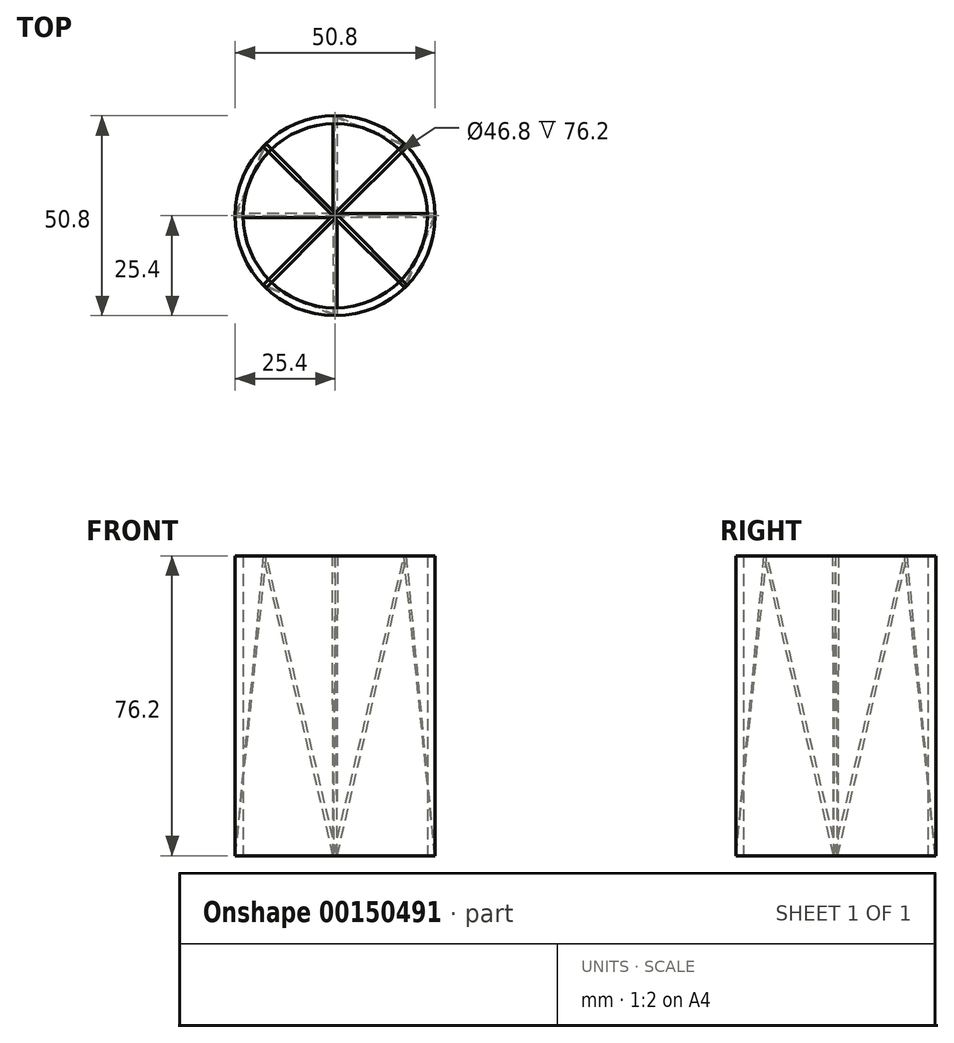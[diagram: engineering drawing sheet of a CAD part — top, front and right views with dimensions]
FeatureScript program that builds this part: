
annotation { "Feature Type Name" : "Feature", "Feature Type Description" : "" }
export const myFeature = defineFeature(function(context is Context, id is Id, definition is map)
    precondition{}
    {
        {
            var Q0;
            Q0=qCreatedBy(makeId("Top.planeOp"),FACE);
            var sketch = newSketch(context, id + "F0", { "sketchPlane" : qUnion([Q0])});
            skCircle(sketch, "E0", {"center": v(0, 0) * mm, "radius": 23.4 * mm});
            skCircle(sketch, "E1", {"center": v(0, 0) * mm, "radius": 25.4 * mm});
            skSolve(sketch);
        }
        {
            var Q0;
            Q0=makeQuery(id+"F0.imprint","IMPRINT",FACE,{"disambiguationData":[TD([[makeQuery(id+"F0.imprint","IMPRINT",EDGE,{"derivedFrom":sQuery(id+"F0.wireOp",EDGE,"E0")}),-1.0]])]});
            extrude(context, id + "F1", {"entities" : qUnion([Q0]), "depth" : 76.2 * mm});
        }
        {
            var Q0;
            Q0=qCreatedBy(makeId("Top.planeOp"),FACE);
            var sketch = newSketch(context, id + "F2", { "sketchPlane" : qUnion([Q0])});
            skLineSegment(sketch, "E2.bottom", {"start": v(-0.5, 25.31) * mm, "end": v(0.5, 25.31) * mm});
            skLineSegment(sketch, "E2.top", {"start": v(-0.5, -25.31) * mm, "end": v(0.5, -25.31) * mm});
            skLineSegment(sketch, "E2.left", {"start": v(-0.5, 25.31) * mm, "end": v(-0.5, -25.31) * mm});
            skLineSegment(sketch, "E2.right", {"start": v(0.5, 25.32) * mm, "end": v(0.5, -25.31) * mm});
            skPoint(sketch, "E2.middle", {"position": v(0, 0) * mm});
            skLineSegment(sketch, "E3.bottom", {"start": v(25.32, 0.5) * mm, "end": v(-25.32, 0.5) * mm});
            skLineSegment(sketch, "E3.top", {"start": v(25.32, -0.5) * mm, "end": v(-25.32, -0.5) * mm});
            skLineSegment(sketch, "E3.left", {"start": v(25.32, 0.5) * mm, "end": v(25.32, -0.5) * mm});
            skLineSegment(sketch, "E4", {"start": v(-25.32, 0.5) * mm, "end": v(-25.32, -0.5) * mm});
            skSolve(sketch);
        }
        {
            var Q0;
            Q0=qCreatedBy(makeId("Top.planeOp"),FACE);
            cPlane(context, id + "F3", {"entities" : qUnion([Q0]), "cplaneType" : CPlaneType.OFFSET, "offset" : 76.2 * mm, "width" : 152.4 * mm, "height" : 152.4 * mm});
        }
        {
            var Q0;
            Q0=qCreatedBy(id+"F3.planeOp",FACE);
            var sketch = newSketch(context, id + "F4", { "sketchPlane" : qUnion([Q0])});
            skLineSegment(sketch, "E5.bottom", {"start": v(-18.17, 17.46) * mm, "end": v(-17.46, 18.17) * mm});
            skLineSegment(sketch, "E5.top", {"start": v(17.46, -18.17) * mm, "end": v(18.17, -17.46) * mm});
            skLineSegment(sketch, "E5.left", {"start": v(-18.17, 17.46) * mm, "end": v(17.46, -18.17) * mm});
            skLineSegment(sketch, "E5.right", {"start": v(-17.46, 18.17) * mm, "end": v(18.17, -17.46) * mm});
            skPoint(sketch, "E5.middle", {"position": v(0, 0) * mm});
            skLineSegment(sketch, "E6.bottom", {"start": v(17.5, 18.2) * mm, "end": v(-18.2, -17.5) * mm});
            skLineSegment(sketch, "E6.top", {"start": v(18.2, 17.5) * mm, "end": v(-17.5, -18.2) * mm});
            skLineSegment(sketch, "E6.left", {"start": v(17.5, 18.2) * mm, "end": v(18.2, 17.5) * mm});
            skLineSegment(sketch, "E6.right", {"start": v(-18.2, -17.5) * mm, "end": v(-17.5, -18.2) * mm});
            skSolve(sketch);
        }
        {
            var Q0;
            {var subQ0=sQuery(id+"F2.wireOp",EDGE,"E2.top");Q0=makeQuery(id+"F2.imprint","IMPRINT",FACE,{"disambiguationData":[TD([[makeQuery(id+"F2.imprint","IMPRINT",EDGE,{"derivedFrom":subQ0}),1.0]])]});}
            var Q1;
            {var subQ5=sQuery(id+"F4.wireOp",EDGE,"E6.right");Q1=makeQuery(id+"F4.imprint","IMPRINT",FACE,{"disambiguationData":[TD([[makeQuery(id+"F4.imprint","IMPRINT",EDGE,{"derivedFrom":subQ5}),1.0]])]});}
            loft(context, id + "F5", {"sheetProfilesArray" : [{ "sheetProfileEntities" : qUnion([Q0]) }, { "sheetProfileEntities" : qUnion([Q1]) }]});
        }
        {
            var Q0;
            {var subQ5=sQuery(id+"F2.wireOp",EDGE,"E4");Q0=makeQuery(id+"F2.imprint","IMPRINT",FACE,{"disambiguationData":[TD([[makeQuery(id+"F2.imprint","IMPRINT",EDGE,{"derivedFrom":subQ5}),1.0]])]});}
            var Q1;
            {var subQ0=sQuery(id+"F4.wireOp",EDGE,"E5.bottom");Q1=makeQuery(id+"F4.imprint","IMPRINT",FACE,{"disambiguationData":[TD([[makeQuery(id+"F4.imprint","IMPRINT",EDGE,{"derivedFrom":subQ0}),-1.0]])]});}
            loft(context, id + "F6", {"sheetProfilesArray" : [{ "sheetProfileEntities" : qUnion([Q0]) }, { "sheetProfileEntities" : qUnion([Q1]) }]});
        }
        {
            var Q0;
            {var subQ0=sQuery(id+"F2.wireOp",EDGE,"E2.bottom");Q0=makeQuery(id+"F2.imprint","IMPRINT",FACE,{"disambiguationData":[TD([[makeQuery(id+"F2.imprint","IMPRINT",EDGE,{"derivedFrom":subQ0}),-1.0]])]});}
            var Q1;
            {var subQ5=sQuery(id+"F4.wireOp",EDGE,"E6.left");Q1=makeQuery(id+"F4.imprint","IMPRINT",FACE,{"disambiguationData":[TD([[makeQuery(id+"F4.imprint","IMPRINT",EDGE,{"derivedFrom":subQ5}),-1.0]])]});}
            loft(context, id + "F7", {"sheetProfilesArray" : [{ "sheetProfileEntities" : qUnion([Q0]) }, { "sheetProfileEntities" : qUnion([Q1]) }]});
        }
        {
            var Q0;
            {var subQ5=sQuery(id+"F2.wireOp",EDGE,"E3.left");Q0=makeQuery(id+"F2.imprint","IMPRINT",FACE,{"disambiguationData":[TD([[makeQuery(id+"F2.imprint","IMPRINT",EDGE,{"derivedFrom":subQ5}),-1.0]])]});}
            var Q1;
            {var subQ0=sQuery(id+"F4.wireOp",EDGE,"E5.top");Q1=makeQuery(id+"F4.imprint","IMPRINT",FACE,{"disambiguationData":[TD([[makeQuery(id+"F4.imprint","IMPRINT",EDGE,{"derivedFrom":subQ0}),1.0]])]});}
            loft(context, id + "F8", {"sheetProfilesArray" : [{ "sheetProfileEntities" : qUnion([Q0]) }, { "sheetProfileEntities" : qUnion([Q1]) }]});
        }
        {
            var Q0;
            {var subQ0=sQuery(id+"F4.wireOp",EDGE,"E6.bottom");var subQ1=sQuery(id+"F4.wireOp",EDGE,"E5.left");var subQ2=makeQuery(id+"F4.imprint","INTERSECT",VERTEX,{"derivedFrom":[subQ1,subQ0]});Q0=makeQuery(id+"F4.imprint","IMPRINT",FACE,{"disambiguationData":[TD([[makeQuery(id+"F4.imprint","IMPRINT",EDGE,{"disambiguationData":[TD([[subQ2,-1.0]])],"derivedFrom":subQ1}),1.0]])]});}
            var Q1;
            {var subQ0=sQuery(id+"F2.wireOp",EDGE,"E3.bottom");var subQ1=sQuery(id+"F2.wireOp",EDGE,"E2.left");var subQ2=makeQuery(id+"F2.imprint","INTERSECT",VERTEX,{"derivedFrom":[subQ1,subQ0]});Q1=makeQuery(id+"F2.imprint","IMPRINT",FACE,{"disambiguationData":[TD([[makeQuery(id+"F2.imprint","IMPRINT",EDGE,{"disambiguationData":[TD([[subQ2,-1.0]])],"derivedFrom":subQ1}),1.0]])]});}
            loft(context, id + "F9", {"sheetProfilesArray" : [{ "sheetProfileEntities" : qUnion([Q0]) }, { "sheetProfileEntities" : qUnion([Q1]) }]});
        }
    });
